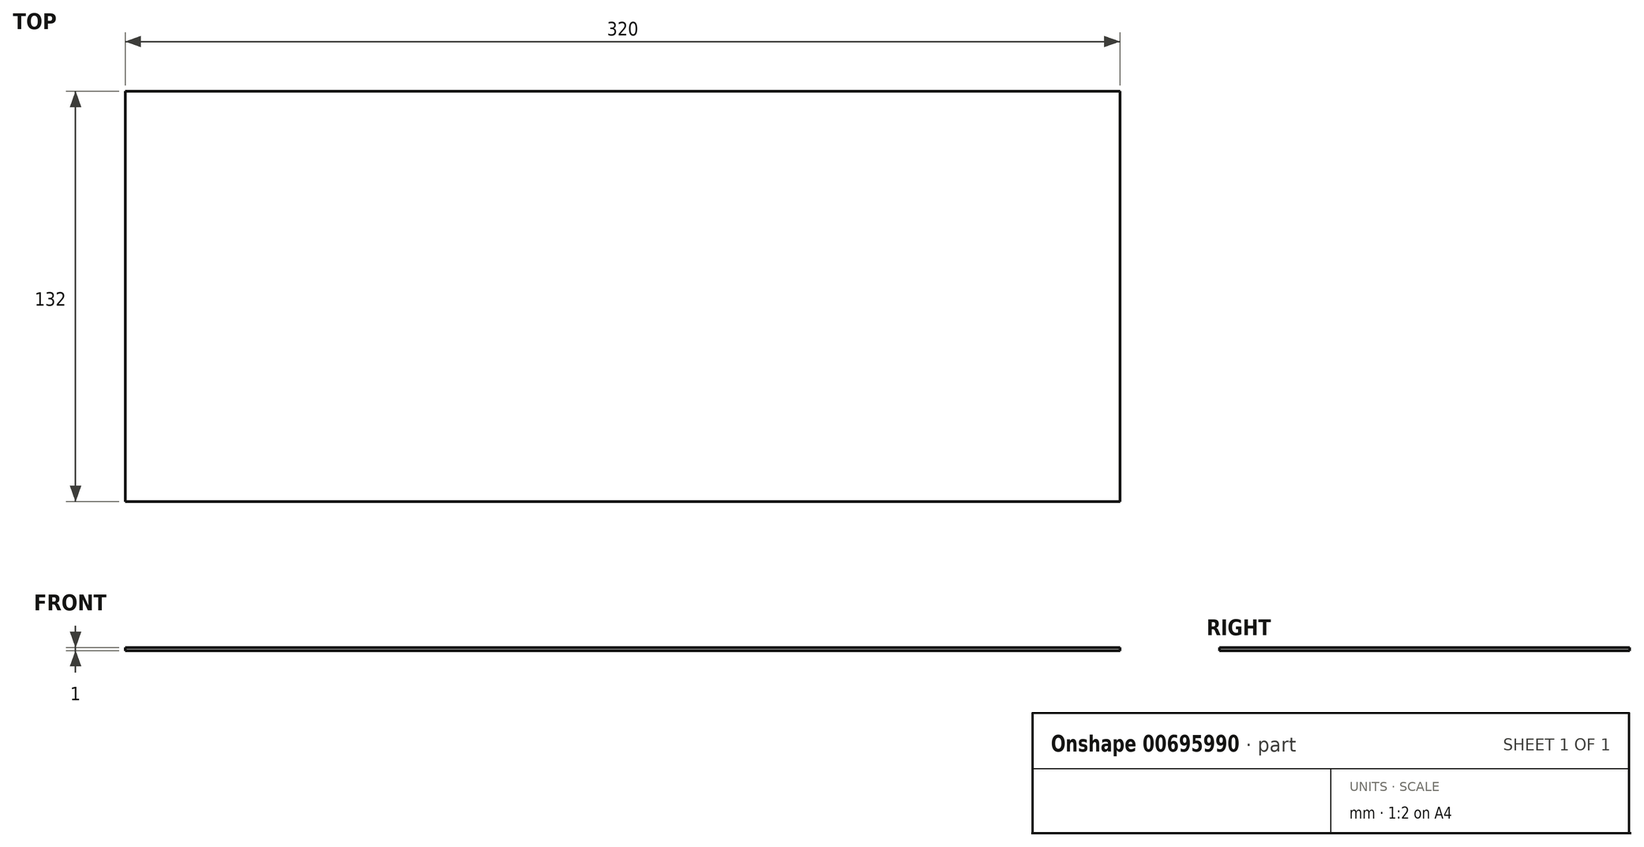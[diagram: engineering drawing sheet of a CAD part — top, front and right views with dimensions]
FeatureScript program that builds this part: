
annotation { "Feature Type Name" : "Feature", "Feature Type Description" : "" }
export const myFeature = defineFeature(function(context is Context, id is Id, definition is map)
    precondition{}
    {
        {
            var Q0;
            Q0=qCreatedBy(makeId("Top.planeOp"),FACE);
            var sketch = newSketch(context, id + "F0", { "sketchPlane" : qUnion([Q0])});
            skLineSegment(sketch, "E0.bottom", {"start": v(169.1, -151.92) * mm, "end": v(-150.9, -151.92) * mm});
            skLineSegment(sketch, "E0.top", {"start": v(169.1, -19.92) * mm, "end": v(-150.9, -19.92) * mm});
            skLineSegment(sketch, "E0.left", {"start": v(169.1, -151.92) * mm, "end": v(169.1, -19.92) * mm});
            skLineSegment(sketch, "E0.right", {"start": v(-150.9, -151.92) * mm, "end": v(-150.9, -19.92) * mm});
            skSolve(sketch);
        }
        {
            var Q0;
            Q0=makeQuery(id+"F0.imprint","IMPRINT",FACE,{"disambiguationData":[TD([[makeQuery(id+"F0.imprint","IMPRINT",EDGE,{"derivedFrom":sQuery(id+"F0.wireOp",EDGE,"E0.bottom")}),-1.0]])]});
            extrude(context, id + "F1", {"entities" : qUnion([Q0]), "depth" : 1 * mm, "offsetDistance" : 25 * mm});
        }
    });
